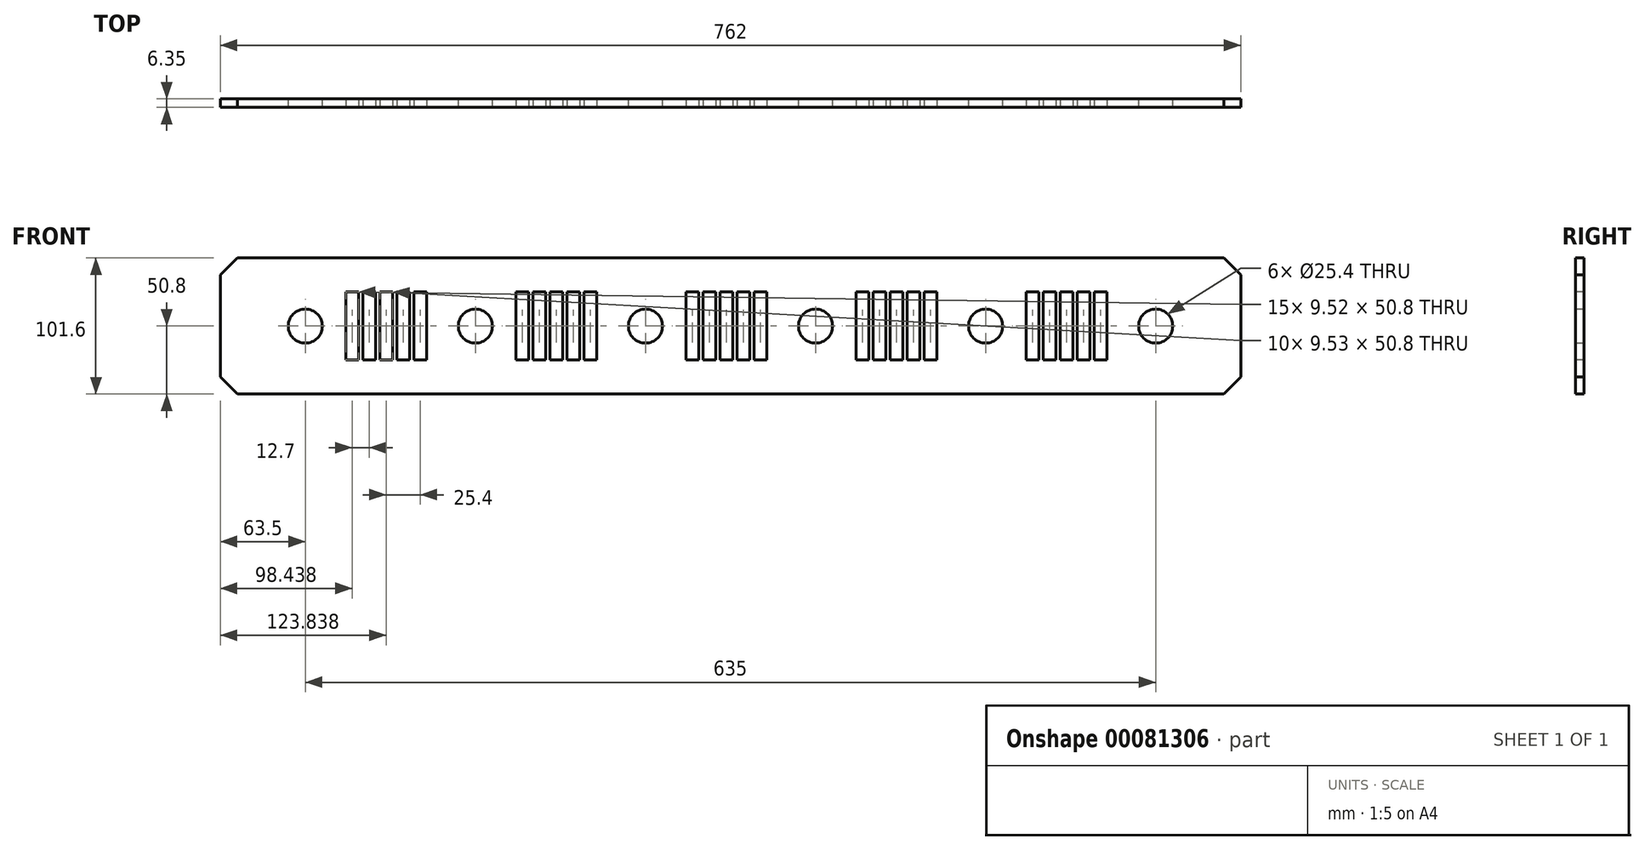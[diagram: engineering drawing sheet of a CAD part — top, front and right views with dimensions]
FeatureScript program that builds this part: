
annotation { "Feature Type Name" : "Feature", "Feature Type Description" : "" }
export const myFeature = defineFeature(function(context is Context, id is Id, definition is map)
    precondition{}
    {
        {
            var Q0;
            Q0=qCreatedBy(makeId("Front.planeOp"),FACE);
            var sketch = newSketch(context, id + "F0", { "sketchPlane" : qUnion([Q0])});
            skLineSegment(sketch, "E0.bottom", {"start": v(0, 0) * mm, "end": v(762, 0) * mm});
            skLineSegment(sketch, "E0.top", {"start": v(0, 101.6) * mm, "end": v(762, 101.6) * mm});
            skLineSegment(sketch, "E0.left", {"start": v(0, 0) * mm, "end": v(0, 101.6) * mm});
            skLineSegment(sketch, "E0.right", {"start": v(762, 0) * mm, "end": v(762, 101.6) * mm});
            skCircle(sketch, "E1", {"center": v(63.5, 50.8) * mm, "radius": 12.7 * mm});
            skPoint(sketch, "E1.centerSnap0", {"position": v(0, 50.8) * mm});
            skCircle(sketch, "E2", {"center": v(190.5, 50.8) * mm, "radius": 12.7 * mm});
            skCircle(sketch, "E3", {"center": v(317.5, 50.8) * mm, "radius": 12.7 * mm});
            skCircle(sketch, "E4", {"center": v(444.5, 50.8) * mm, "radius": 12.7 * mm});
            skCircle(sketch, "E5", {"center": v(571.5, 50.8) * mm, "radius": 12.7 * mm});
            skCircle(sketch, "E6", {"center": v(698.5, 50.8) * mm, "radius": 12.7 * mm});
            skSolve(sketch);
        }
        {
            var Q0;
            Q0 = qSketchRegion(id + "F0", true);
            extrude(context, id + "F1", {"entities" : qUnion([Q0]), "depth" : 6.35 * mm});
        }
        {
            var Q0;
            Q0=makeQuery(id+"F1.opExtrude","SWEPT_EDGE",EDGE,{"disambiguationData":[OSD([sQuery(id+"F0.wireOp",EDGE,"E0.top"),sQuery(id+"F0.wireOp",EDGE,"E0.left")])]});
            var Q1;
            Q1=makeQuery(id+"F1.opExtrude","SWEPT_EDGE",EDGE,{"disambiguationData":[OSD([sQuery(id+"F0.wireOp",EDGE,"E0.bottom"),sQuery(id+"F0.wireOp",EDGE,"E0.left")])]});
            var Q2;
            Q2=makeQuery(id+"F1.opExtrude","SWEPT_EDGE",EDGE,{"disambiguationData":[OSD([sQuery(id+"F0.wireOp",EDGE,"E0.bottom"),sQuery(id+"F0.wireOp",EDGE,"E0.right")])]});
            var Q3;
            Q3=makeQuery(id+"F1.opExtrude","SWEPT_EDGE",EDGE,{"disambiguationData":[OSD([sQuery(id+"F0.wireOp",EDGE,"E0.top"),sQuery(id+"F0.wireOp",EDGE,"E0.right")])]});
            chamfer(context, id + "F2", {"entities" : qUnion([Q0, Q1, Q2, Q3]), "width" : 12.7 * mm, "tangentPropagation" : true});
        }
        {
            var Q0;
            Q0=makeQuery(id+"F1.opExtrude","CAP_FACE",FACE,{"disambiguationData":[OSD([sQuery(id+"F0.wireOp",EDGE,"E0.bottom"),sQuery(id+"F0.wireOp",EDGE,"E0.top"),sQuery(id+"F0.wireOp",EDGE,"E0.left"),sQuery(id+"F0.wireOp",EDGE,"E0.right"),sQuery(id+"F0.wireOp",EDGE,"E1"),sQuery(id+"F0.wireOp",EDGE,"E2"),sQuery(id+"F0.wireOp",EDGE,"E3"),sQuery(id+"F0.wireOp",EDGE,"E4"),sQuery(id+"F0.wireOp",EDGE,"E5"),sQuery(id+"F0.wireOp",EDGE,"E6")])],"isStart":false});
            var sketch = newSketch(context, id + "F3", { "sketchPlane" : qUnion([Q0])});
            skLineSegment(sketch, "E7.bottom", {"start": v(93.68, 25.4) * mm, "end": v(103.2, 25.4) * mm});
            skLineSegment(sketch, "E7.top", {"start": v(93.68, 76.2) * mm, "end": v(103.2, 76.2) * mm});
            skLineSegment(sketch, "E7.left", {"start": v(93.68, 25.4) * mm, "end": v(93.68, 76.2) * mm});
            skLineSegment(sketch, "E7.right", {"start": v(103.2, 25.4) * mm, "end": v(103.2, 76.2) * mm});
            skLineSegment(sketch, "E8.1.0.0", {"start": v(106.38, 25.4) * mm, "end": v(115.9, 25.4) * mm});
            skLineSegment(sketch, "E8.1.0.1", {"start": v(115.9, 25.4) * mm, "end": v(115.9, 76.2) * mm});
            skLineSegment(sketch, "E8.1.0.2", {"start": v(106.38, 25.4) * mm, "end": v(106.38, 76.2) * mm});
            skLineSegment(sketch, "E8.1.0.3", {"start": v(106.38, 76.2) * mm, "end": v(115.9, 76.2) * mm});
            skLineSegment(sketch, "E8.2.0.0", {"start": v(119.08, 25.4) * mm, "end": v(128.6, 25.4) * mm});
            skLineSegment(sketch, "E8.2.0.1", {"start": v(128.6, 25.4) * mm, "end": v(128.6, 76.2) * mm});
            skLineSegment(sketch, "E8.2.0.2", {"start": v(119.08, 25.4) * mm, "end": v(119.08, 76.2) * mm});
            skLineSegment(sketch, "E8.2.0.3", {"start": v(119.08, 76.2) * mm, "end": v(128.6, 76.2) * mm});
            skLineSegment(sketch, "E8.3.0.0", {"start": v(131.78, 25.4) * mm, "end": v(141.3, 25.4) * mm});
            skLineSegment(sketch, "E8.3.0.1", {"start": v(141.3, 25.4) * mm, "end": v(141.3, 76.2) * mm});
            skLineSegment(sketch, "E8.3.0.2", {"start": v(131.78, 25.4) * mm, "end": v(131.78, 76.2) * mm});
            skLineSegment(sketch, "E8.3.0.3", {"start": v(131.78, 76.2) * mm, "end": v(141.3, 76.2) * mm});
            skLineSegment(sketch, "E8.4.0.0", {"start": v(144.48, 25.4) * mm, "end": v(154, 25.4) * mm});
            skLineSegment(sketch, "E8.4.0.1", {"start": v(154, 25.4) * mm, "end": v(154, 76.2) * mm});
            skLineSegment(sketch, "E8.4.0.2", {"start": v(144.48, 25.4) * mm, "end": v(144.48, 76.2) * mm});
            skLineSegment(sketch, "E8.4.0.3", {"start": v(144.48, 76.2) * mm, "end": v(154, 76.2) * mm});
            skLineSegment(sketch, "E8.direction1", {"start": v(93.68, 25.4) * mm, "end": v(106.38, 25.4) * mm, "construction": true});
            skLineSegment(sketch, "E9.bottom", {"start": v(220.68, 25.4) * mm, "end": v(230.2, 25.4) * mm});
            skLineSegment(sketch, "E9.top", {"start": v(220.68, 76.2) * mm, "end": v(230.2, 76.2) * mm});
            skLineSegment(sketch, "E9.left", {"start": v(220.68, 25.4) * mm, "end": v(220.68, 76.2) * mm});
            skLineSegment(sketch, "E9.right", {"start": v(230.2, 25.4) * mm, "end": v(230.2, 76.2) * mm});
            skLineSegment(sketch, "E10.1.0.0", {"start": v(233.38, 25.4) * mm, "end": v(242.9, 25.4) * mm});
            skLineSegment(sketch, "E10.1.0.1", {"start": v(242.9, 25.4) * mm, "end": v(242.9, 76.2) * mm});
            skLineSegment(sketch, "E10.1.0.2", {"start": v(233.38, 25.4) * mm, "end": v(233.38, 76.2) * mm});
            skLineSegment(sketch, "E10.1.0.3", {"start": v(233.38, 76.2) * mm, "end": v(242.9, 76.2) * mm});
            skLineSegment(sketch, "E10.2.0.0", {"start": v(246.08, 25.4) * mm, "end": v(255.6, 25.4) * mm});
            skLineSegment(sketch, "E10.2.0.1", {"start": v(255.6, 25.4) * mm, "end": v(255.6, 76.2) * mm});
            skLineSegment(sketch, "E10.2.0.2", {"start": v(246.08, 25.4) * mm, "end": v(246.08, 76.2) * mm});
            skLineSegment(sketch, "E10.2.0.3", {"start": v(246.08, 76.2) * mm, "end": v(255.6, 76.2) * mm});
            skLineSegment(sketch, "E10.3.0.0", {"start": v(258.78, 25.4) * mm, "end": v(268.3, 25.4) * mm});
            skLineSegment(sketch, "E10.3.0.1", {"start": v(268.3, 25.4) * mm, "end": v(268.3, 76.2) * mm});
            skLineSegment(sketch, "E10.3.0.2", {"start": v(258.78, 25.4) * mm, "end": v(258.78, 76.2) * mm});
            skLineSegment(sketch, "E10.3.0.3", {"start": v(258.78, 76.2) * mm, "end": v(268.3, 76.2) * mm});
            skLineSegment(sketch, "E10.4.0.0", {"start": v(271.48, 25.4) * mm, "end": v(281, 25.4) * mm});
            skLineSegment(sketch, "E10.4.0.1", {"start": v(281, 25.4) * mm, "end": v(281, 76.2) * mm});
            skLineSegment(sketch, "E10.4.0.2", {"start": v(271.48, 25.4) * mm, "end": v(271.48, 76.2) * mm});
            skLineSegment(sketch, "E10.4.0.3", {"start": v(271.48, 76.2) * mm, "end": v(281, 76.2) * mm});
            skLineSegment(sketch, "E10.direction1", {"start": v(220.68, 25.4) * mm, "end": v(233.38, 25.4) * mm, "construction": true});
            skLineSegment(sketch, "E11.bottom", {"start": v(347.68, 25.4) * mm, "end": v(357.2, 25.4) * mm});
            skLineSegment(sketch, "E11.top", {"start": v(347.68, 76.2) * mm, "end": v(357.2, 76.2) * mm});
            skLineSegment(sketch, "E11.left", {"start": v(347.68, 25.4) * mm, "end": v(347.68, 76.2) * mm});
            skLineSegment(sketch, "E11.right", {"start": v(357.2, 25.4) * mm, "end": v(357.2, 76.2) * mm});
            skLineSegment(sketch, "E12.1.0.0", {"start": v(360.38, 25.4) * mm, "end": v(369.9, 25.4) * mm});
            skLineSegment(sketch, "E12.1.0.1", {"start": v(369.9, 25.4) * mm, "end": v(369.9, 76.2) * mm});
            skLineSegment(sketch, "E12.1.0.2", {"start": v(360.38, 25.4) * mm, "end": v(360.38, 76.2) * mm});
            skLineSegment(sketch, "E12.1.0.3", {"start": v(360.38, 76.2) * mm, "end": v(369.9, 76.2) * mm});
            skLineSegment(sketch, "E12.2.0.0", {"start": v(373.08, 25.4) * mm, "end": v(382.6, 25.4) * mm});
            skLineSegment(sketch, "E12.2.0.1", {"start": v(382.6, 25.4) * mm, "end": v(382.6, 76.2) * mm});
            skLineSegment(sketch, "E12.2.0.2", {"start": v(373.08, 25.4) * mm, "end": v(373.08, 76.2) * mm});
            skLineSegment(sketch, "E12.2.0.3", {"start": v(373.08, 76.2) * mm, "end": v(382.6, 76.2) * mm});
            skLineSegment(sketch, "E12.3.0.0", {"start": v(385.78, 25.4) * mm, "end": v(395.3, 25.4) * mm});
            skLineSegment(sketch, "E12.3.0.1", {"start": v(395.3, 25.4) * mm, "end": v(395.3, 76.2) * mm});
            skLineSegment(sketch, "E12.3.0.2", {"start": v(385.78, 25.4) * mm, "end": v(385.78, 76.2) * mm});
            skLineSegment(sketch, "E12.3.0.3", {"start": v(385.78, 76.2) * mm, "end": v(395.3, 76.2) * mm});
            skLineSegment(sketch, "E12.4.0.0", {"start": v(398.48, 25.4) * mm, "end": v(408, 25.4) * mm});
            skLineSegment(sketch, "E12.4.0.1", {"start": v(408, 25.4) * mm, "end": v(408, 76.2) * mm});
            skLineSegment(sketch, "E12.4.0.2", {"start": v(398.48, 25.4) * mm, "end": v(398.48, 76.2) * mm});
            skLineSegment(sketch, "E12.4.0.3", {"start": v(398.48, 76.2) * mm, "end": v(408, 76.2) * mm});
            skLineSegment(sketch, "E12.direction1", {"start": v(347.68, 25.4) * mm, "end": v(360.38, 25.4) * mm, "construction": true});
            skLineSegment(sketch, "E13.bottom", {"start": v(474.68, 25.4) * mm, "end": v(484.2, 25.4) * mm});
            skLineSegment(sketch, "E13.top", {"start": v(474.68, 76.2) * mm, "end": v(484.2, 76.2) * mm});
            skLineSegment(sketch, "E13.left", {"start": v(474.68, 25.4) * mm, "end": v(474.68, 76.2) * mm});
            skLineSegment(sketch, "E13.right", {"start": v(484.2, 25.4) * mm, "end": v(484.2, 76.2) * mm});
            skLineSegment(sketch, "E14.1.0.0", {"start": v(487.38, 25.4) * mm, "end": v(496.9, 25.4) * mm});
            skLineSegment(sketch, "E14.1.0.1", {"start": v(496.9, 25.4) * mm, "end": v(496.9, 76.2) * mm});
            skLineSegment(sketch, "E14.1.0.2", {"start": v(487.38, 25.4) * mm, "end": v(487.38, 76.2) * mm});
            skLineSegment(sketch, "E14.1.0.3", {"start": v(487.38, 76.2) * mm, "end": v(496.9, 76.2) * mm});
            skLineSegment(sketch, "E14.2.0.0", {"start": v(500.08, 25.4) * mm, "end": v(509.6, 25.4) * mm});
            skLineSegment(sketch, "E14.2.0.1", {"start": v(509.6, 25.4) * mm, "end": v(509.6, 76.2) * mm});
            skLineSegment(sketch, "E14.2.0.2", {"start": v(500.08, 25.4) * mm, "end": v(500.08, 76.2) * mm});
            skLineSegment(sketch, "E14.2.0.3", {"start": v(500.08, 76.2) * mm, "end": v(509.6, 76.2) * mm});
            skLineSegment(sketch, "E14.3.0.0", {"start": v(512.78, 25.4) * mm, "end": v(522.3, 25.4) * mm});
            skLineSegment(sketch, "E14.3.0.1", {"start": v(522.3, 25.4) * mm, "end": v(522.3, 76.2) * mm});
            skLineSegment(sketch, "E14.3.0.2", {"start": v(512.78, 25.4) * mm, "end": v(512.78, 76.2) * mm});
            skLineSegment(sketch, "E14.3.0.3", {"start": v(512.78, 76.2) * mm, "end": v(522.3, 76.2) * mm});
            skLineSegment(sketch, "E14.4.0.0", {"start": v(525.48, 25.4) * mm, "end": v(535, 25.4) * mm});
            skLineSegment(sketch, "E14.4.0.1", {"start": v(535, 25.4) * mm, "end": v(535, 76.2) * mm});
            skLineSegment(sketch, "E14.4.0.2", {"start": v(525.48, 25.4) * mm, "end": v(525.48, 76.2) * mm});
            skLineSegment(sketch, "E14.4.0.3", {"start": v(525.48, 76.2) * mm, "end": v(535, 76.2) * mm});
            skLineSegment(sketch, "E14.direction1", {"start": v(474.68, 25.4) * mm, "end": v(487.38, 25.4) * mm, "construction": true});
            skLineSegment(sketch, "E15.bottom", {"start": v(601.68, 25.4) * mm, "end": v(611.2, 25.4) * mm});
            skLineSegment(sketch, "E15.top", {"start": v(601.68, 76.2) * mm, "end": v(611.2, 76.2) * mm});
            skLineSegment(sketch, "E15.left", {"start": v(601.68, 25.4) * mm, "end": v(601.68, 76.2) * mm});
            skLineSegment(sketch, "E15.right", {"start": v(611.2, 25.4) * mm, "end": v(611.2, 76.2) * mm});
            skLineSegment(sketch, "E16.1.0.0", {"start": v(614.38, 25.4) * mm, "end": v(623.9, 25.4) * mm});
            skLineSegment(sketch, "E16.1.0.1", {"start": v(623.9, 25.4) * mm, "end": v(623.9, 76.2) * mm});
            skLineSegment(sketch, "E16.1.0.2", {"start": v(614.38, 25.4) * mm, "end": v(614.38, 76.2) * mm});
            skLineSegment(sketch, "E16.1.0.3", {"start": v(614.38, 76.2) * mm, "end": v(623.9, 76.2) * mm});
            skLineSegment(sketch, "E16.2.0.0", {"start": v(627.08, 25.4) * mm, "end": v(636.6, 25.4) * mm});
            skLineSegment(sketch, "E16.2.0.1", {"start": v(636.6, 25.4) * mm, "end": v(636.6, 76.2) * mm});
            skLineSegment(sketch, "E16.2.0.2", {"start": v(627.08, 25.4) * mm, "end": v(627.08, 76.2) * mm});
            skLineSegment(sketch, "E16.2.0.3", {"start": v(627.08, 76.2) * mm, "end": v(636.6, 76.2) * mm});
            skLineSegment(sketch, "E16.3.0.0", {"start": v(639.78, 25.4) * mm, "end": v(649.3, 25.4) * mm});
            skLineSegment(sketch, "E16.3.0.1", {"start": v(649.3, 25.4) * mm, "end": v(649.3, 76.2) * mm});
            skLineSegment(sketch, "E16.3.0.2", {"start": v(639.78, 25.4) * mm, "end": v(639.78, 76.2) * mm});
            skLineSegment(sketch, "E16.3.0.3", {"start": v(639.78, 76.2) * mm, "end": v(649.3, 76.2) * mm});
            skLineSegment(sketch, "E16.4.0.0", {"start": v(652.48, 25.4) * mm, "end": v(662, 25.4) * mm});
            skLineSegment(sketch, "E16.4.0.1", {"start": v(662, 25.4) * mm, "end": v(662, 76.2) * mm});
            skLineSegment(sketch, "E16.4.0.2", {"start": v(652.48, 25.4) * mm, "end": v(652.48, 76.2) * mm});
            skLineSegment(sketch, "E16.4.0.3", {"start": v(652.48, 76.2) * mm, "end": v(662, 76.2) * mm});
            skLineSegment(sketch, "E16.direction1", {"start": v(601.68, 25.4) * mm, "end": v(614.38, 25.4) * mm, "construction": true});
            skSolve(sketch);
        }
        {
            var Q0;
            Q0 = qSketchRegion(id + "F3", true);
            extrude(context, id + "F4", {"entities" : qUnion([Q0]), "operationType" : NewBodyOperationType.REMOVE, "endBound" : BoundingType.THROUGH_ALL, "oppositeDirection" : true, "depth" : 25.4 * mm});
        }
    });
